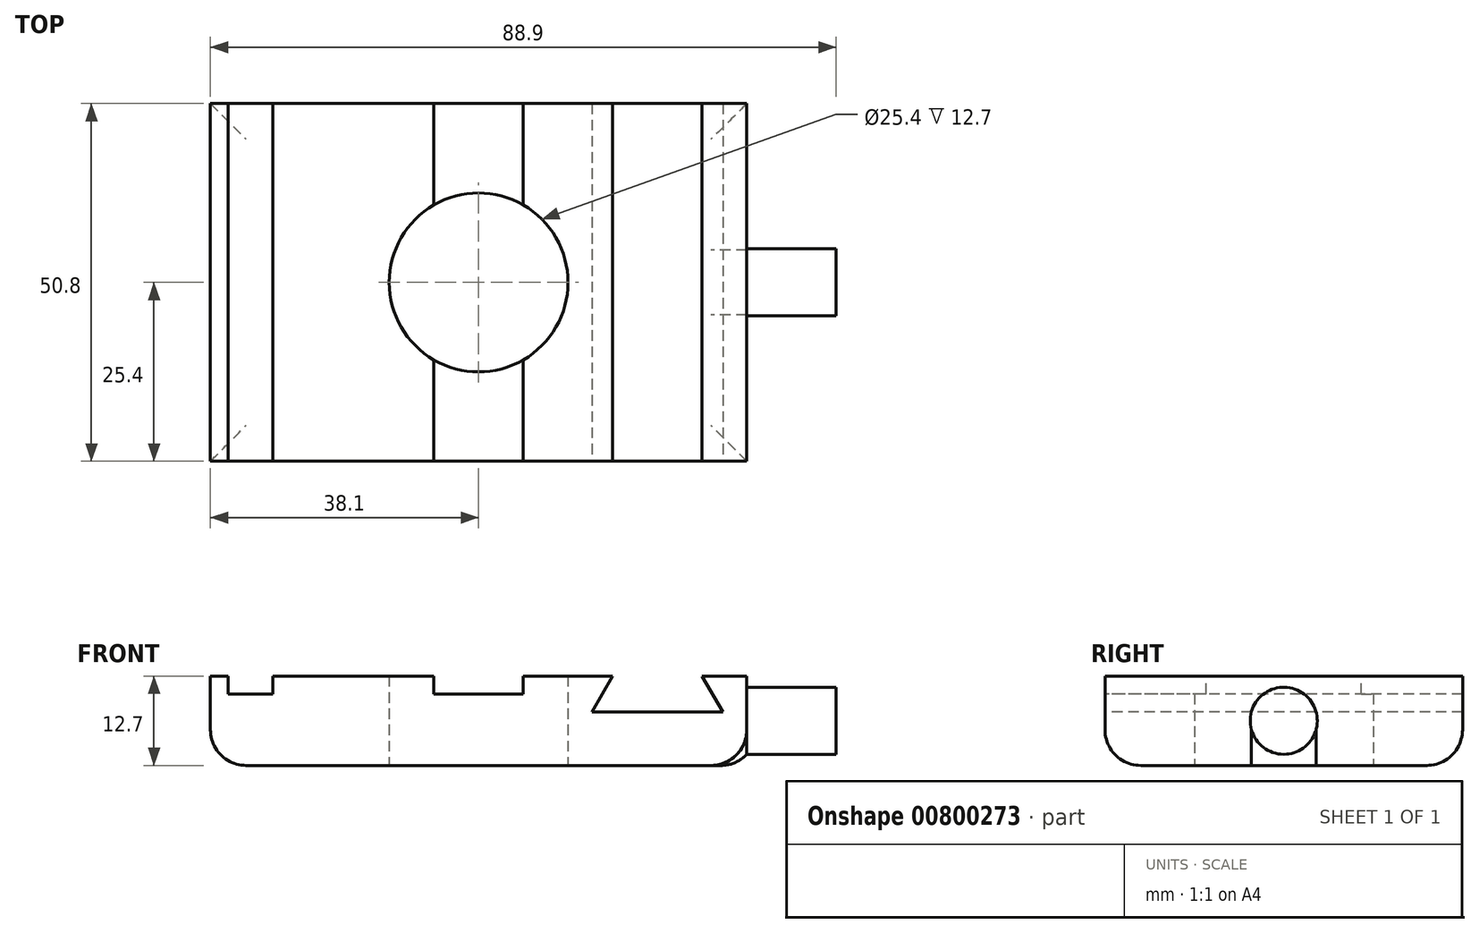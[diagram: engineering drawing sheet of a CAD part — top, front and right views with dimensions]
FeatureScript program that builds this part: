
annotation { "Feature Type Name" : "Feature", "Feature Type Description" : "" }
export const myFeature = defineFeature(function(context is Context, id is Id, definition is map)
    precondition{}
    {
        {
            var Q0;
            Q0=qCreatedBy(makeId("Top.planeOp"),FACE);
            var sketch = newSketch(context, id + "F0", { "sketchPlane" : qUnion([Q0])});
            skLineSegment(sketch, "E0.bottom", {"start": v(38.1, 25.4) * mm, "end": v(-38.1, 25.4) * mm});
            skLineSegment(sketch, "E0.top", {"start": v(38.1, -25.4) * mm, "end": v(-38.1, -25.4) * mm});
            skLineSegment(sketch, "E0.left", {"start": v(38.1, 25.4) * mm, "end": v(38.1, -25.4) * mm});
            skLineSegment(sketch, "E0.right", {"start": v(-38.1, 25.4) * mm, "end": v(-38.1, -25.4) * mm});
            skPoint(sketch, "E0.middle", {"position": v(0, 0) * mm});
            skCircle(sketch, "E1", {"center": v(0, 0) * mm, "radius": 12.7 * mm});
            skSolve(sketch);
        }
        {
            var Q0;
            Q0=makeQuery(id+"F0.imprint","IMPRINT",FACE,{"disambiguationData":[TD([[makeQuery(id+"F0.imprint","IMPRINT",EDGE,{"derivedFrom":sQuery(id+"F0.wireOp",EDGE,"E0.bottom")}),1.0]])]});
            extrude(context, id + "F1", {"entities" : qUnion([Q0]), "depth" : 12.7 * mm, "offsetDistance" : 25.4 * mm});
        }
        {
            var Q0;
            Q0=makeQuery(id+"F1.opExtrude","CAP_FACE",FACE,{"disambiguationData":[OSD([sQuery(id+"F0.wireOp",EDGE,"E0.bottom"),sQuery(id+"F0.wireOp",EDGE,"E0.top"),sQuery(id+"F0.wireOp",EDGE,"E0.left"),sQuery(id+"F0.wireOp",EDGE,"E0.right"),sQuery(id+"F0.wireOp",EDGE,"E1")])],"isStart":false});
            var sketch = newSketch(context, id + "F2", { "sketchPlane" : qUnion([Q0])});
            skLineSegment(sketch, "E2.bottom", {"start": v(-35.56, 25.4) * mm, "end": v(-29.2, 25.4) * mm});
            skLineSegment(sketch, "E2.top", {"start": v(-35.56, -25.4) * mm, "end": v(-29.2, -25.4) * mm});
            skLineSegment(sketch, "E2.left", {"start": v(-35.56, 25.4) * mm, "end": v(-35.56, -25.4) * mm});
            skLineSegment(sketch, "E2.right", {"start": v(-29.2, 25.4) * mm, "end": v(-29.2, -25.4) * mm});
            skLineSegment(sketch, "E3", {"start": v(-6.35, 25.4) * mm, "end": v(-6.35, -25.4) * mm});
            skLineSegment(sketch, "E4", {"start": v(-6.35, -25.4) * mm, "end": v(6.35, -25.4) * mm});
            skLineSegment(sketch, "E5", {"start": v(6.35, -25.4) * mm, "end": v(6.35, 25.4) * mm});
            skLineSegment(sketch, "E6", {"start": v(6.35, 25.4) * mm, "end": v(-6.35, 25.4) * mm});
            skPoint(sketch, "E7", {"position": v(0, 0) * mm});
            skLineSegment(sketch, "E8", {"start": v(0, 25.4) * mm, "end": v(0, -25.4) * mm, "construction": true});
            skSolve(sketch);
        }
        {
            var Q0;
            Q0=makeQuery(id+"F2.imprint","IMPRINT",FACE,{"disambiguationData":[TD([[makeQuery(id+"F2.imprint","IMPRINT",EDGE,{"derivedFrom":sQuery(id+"F2.wireOp",EDGE,"E2.bottom")}),1.0]])]});
            var Q1;
            {var subQ0=sQuery(id+"F2.wireOp",EDGE,"E4");Q1=makeQuery(id+"F2.imprint","IMPRINT",FACE,{"disambiguationData":[TD([[makeQuery(id+"F2.imprint","IMPRINT",EDGE,{"derivedFrom":subQ0}),-1.0]])]});}
            var Q2;
            {var subQ0=sQuery(id+"F2.wireOp",EDGE,"E6");Q2=makeQuery(id+"F2.imprint","IMPRINT",FACE,{"disambiguationData":[TD([[makeQuery(id+"F2.imprint","IMPRINT",EDGE,{"derivedFrom":subQ0}),1.0]])]});}
            extrude(context, id + "F3", {"entities" : qUnion([Q0, Q1, Q2]), "operationType" : NewBodyOperationType.REMOVE, "oppositeDirection" : true, "depth" : 2.54 * mm, "offsetDistance" : 25.4 * mm});
        }
        {
            var Q0;
            Q0=makeQuery(id+"F1.opExtrude","SWEPT_FACE",FACE,{"disambiguationData":[OSD([sQuery(id+"F0.wireOp",EDGE,"E0.top")])]});
            var sketch = newSketch(context, id + "F4", { "sketchPlane" : qUnion([Q0])});
            skLineSegment(sketch, "E9", {"start": v(19.05, 12.7) * mm, "end": v(16.12, 7.62) * mm});
            skLineSegment(sketch, "E10", {"start": v(16.12, 7.62) * mm, "end": v(34.68, 7.62) * mm});
            skLineSegment(sketch, "E11", {"start": v(34.68, 7.62) * mm, "end": v(31.75, 12.7) * mm});
            skLineSegment(sketch, "E12", {"start": v(31.75, 12.7) * mm, "end": v(19.05, 12.7) * mm});
            skLineSegment(sketch, "E13", {"start": v(25.4, 7.62) * mm, "end": v(25.4, 12.7) * mm, "construction": true});
            skSolve(sketch);
        }
        {
            var Q0;
            Q0=makeQuery(id+"F4.imprint","IMPRINT",FACE,{"disambiguationData":[TD([[makeQuery(id+"F4.imprint","IMPRINT",EDGE,{"derivedFrom":sQuery(id+"F4.wireOp",EDGE,"E9")}),1.0]])]});
            extrude(context, id + "F5", {"entities" : qUnion([Q0]), "operationType" : NewBodyOperationType.REMOVE, "endBound" : BoundingType.THROUGH_ALL, "oppositeDirection" : true, "depth" : 25.4 * mm, "offsetDistance" : 25.4 * mm});
        }
        {
            var Q0;
            Q0=makeQuery(id+"F1.opExtrude","SWEPT_FACE",FACE,{"disambiguationData":[OSD([sQuery(id+"F0.wireOp",EDGE,"E0.left")])]});
            var sketch = newSketch(context, id + "F6", { "sketchPlane" : qUnion([Q0])});
            skCircle(sketch, "E14", {"center": v(0, 6.35) * mm, "radius": 4.76 * mm});
            skPoint(sketch, "E14.centerSnap0", {"position": v(-25.4, 6.35) * mm});
            skPoint(sketch, "E14.centerSnap1", {"position": v(0, 12.7) * mm});
            skSolve(sketch);
        }
        {
            var Q0;
            Q0=makeQuery(id+"F6.imprint","IMPRINT",FACE,{"disambiguationData":[TD([[makeQuery(id+"F6.imprint","IMPRINT",EDGE,{"derivedFrom":sQuery(id+"F6.wireOp",EDGE,"E14")}),1.0]])]});
            extrude(context, id + "F7", {"entities" : qUnion([Q0]), "operationType" : NewBodyOperationType.ADD, "depth" : 12.7 * mm, "offsetDistance" : 25.4 * mm});
        }
        {
            var Q0;
            Q0=makeQuery(id+"F1.opExtrude","CAP_EDGE",EDGE,{"disambiguationData":[OSD([sQuery(id+"F0.wireOp",EDGE,"E0.top")])],"isStart":true});
            var Q1;
            Q1=makeQuery(id+"F1.opExtrude","CAP_EDGE",EDGE,{"disambiguationData":[OSD([sQuery(id+"F0.wireOp",EDGE,"E0.left")])],"isStart":true});
            var Q2;
            Q2=makeQuery(id+"F1.opExtrude","CAP_EDGE",EDGE,{"disambiguationData":[OSD([sQuery(id+"F0.wireOp",EDGE,"E0.bottom")])],"isStart":true});
            var Q3;
            Q3=makeQuery(id+"F1.opExtrude","CAP_EDGE",EDGE,{"disambiguationData":[OSD([sQuery(id+"F0.wireOp",EDGE,"E0.right")])],"isStart":true});
            fillet(context, id + "F8", {"entities" : qUnion([Q0, Q1, Q2, Q3]), "radius" : 5.08 * mm, "tangentPropagation" : true, "allowEdgeOverflow" : false});
        }
    });
